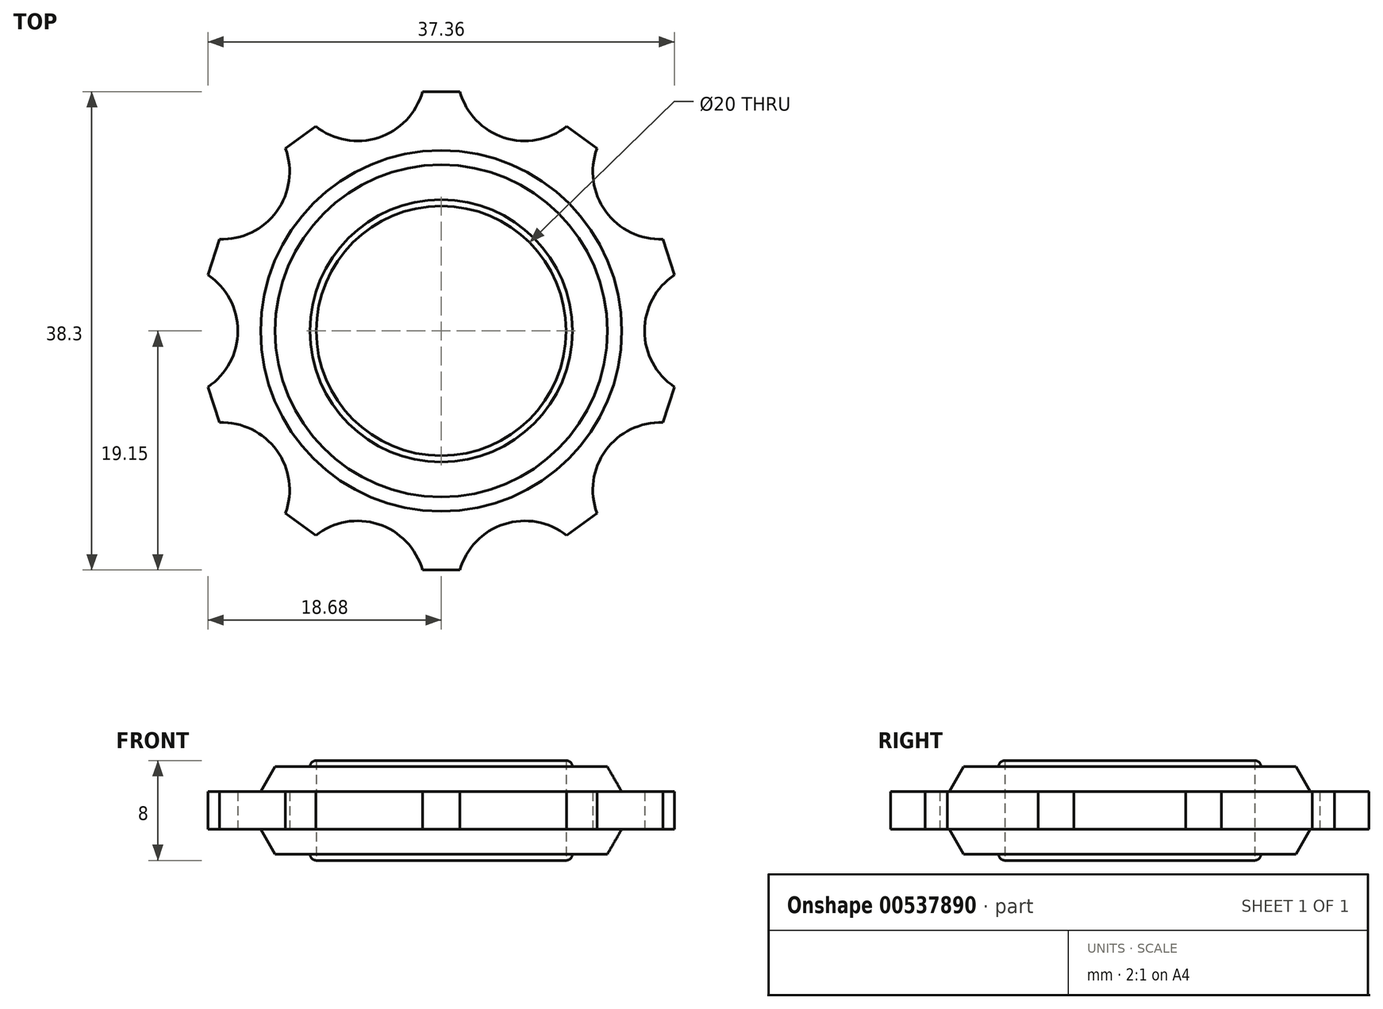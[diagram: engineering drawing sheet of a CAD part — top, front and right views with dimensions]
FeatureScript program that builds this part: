
annotation { "Feature Type Name" : "Feature", "Feature Type Description" : "" }
export const myFeature = defineFeature(function(context is Context, id is Id, definition is map)
    precondition{}
    {
        {
            var Q0;
            Q0=qCreatedBy(makeId("Top.planeOp"),FACE);
            var sketch = newSketch(context, id + "F0", { "sketchPlane" : qUnion([Q0])});
            skCircle(sketch, "E0.cCircle", {"center": v(0, 0) * mm, "radius": 16.27 * mm, "construction": true});
            skLineSegment(sketch, "E0.0", {"start": v(16.27, 5.29) * mm, "end": v(16.27, -5.29) * mm, "construction": true});
            skLineSegment(sketch, "E0.1", {"start": v(16.27, -5.29) * mm, "end": v(10.06, -13.84) * mm, "construction": true});
            skLineSegment(sketch, "E0.2", {"start": v(10.06, -13.84) * mm, "end": v(0, -17.11) * mm, "construction": true});
            skLineSegment(sketch, "E0.3", {"start": v(0, -17.11) * mm, "end": v(-10.06, -13.84) * mm, "construction": true});
            skLineSegment(sketch, "E0.4", {"start": v(-10.06, -13.84) * mm, "end": v(-16.27, -5.29) * mm, "construction": true});
            skLineSegment(sketch, "E0.5", {"start": v(-16.27, -5.29) * mm, "end": v(-16.27, 5.29) * mm, "construction": true});
            skLineSegment(sketch, "E0.6", {"start": v(-16.28, 5.29) * mm, "end": v(-10.06, 13.84) * mm, "construction": true});
            skLineSegment(sketch, "E0.7", {"start": v(-10.06, 13.84) * mm, "end": v(0, 17.11) * mm, "construction": true});
            skLineSegment(sketch, "E0.8", {"start": v(0, 17.11) * mm, "end": v(10.06, 13.84) * mm, "construction": true});
            skLineSegment(sketch, "E0.9", {"start": v(10.06, 13.84) * mm, "end": v(16.27, 5.29) * mm, "construction": true});
            skPoint(sketch, "E0.0.midPoint", {"position": v(16.27, 0) * mm});
            skCircle(sketch, "E1", {"center": v(0, 0) * mm, "radius": 19.15 * mm, "construction": true});
            skLineSegment(sketch, "E2", {"start": v(0, 0) * mm, "end": v(-16.27, -5.29) * mm, "construction": true});
            skLineSegment(sketch, "E3", {"start": v(-16.27, -5.29) * mm, "end": v(-18.21, -5.92) * mm, "construction": true});
            skLineSegment(sketch, "E4", {"start": v(0, 0) * mm, "end": v(-10.06, -13.84) * mm, "construction": true});
            skLineSegment(sketch, "E5", {"start": v(-10.06, -13.84) * mm, "end": v(-11.26, -15.5) * mm, "construction": true});
            skLineSegment(sketch, "E6", {"start": v(0, 0) * mm, "end": v(0, -17.11) * mm, "construction": true});
            skLineSegment(sketch, "E7", {"start": v(0, -17.11) * mm, "end": v(0, -19.15) * mm, "construction": true});
            skLineSegment(sketch, "E8", {"start": v(0, 0) * mm, "end": v(10.06, -13.84) * mm, "construction": true});
            skLineSegment(sketch, "E9", {"start": v(10.06, -13.84) * mm, "end": v(11.26, -15.5) * mm, "construction": true});
            skLineSegment(sketch, "E10", {"start": v(0, 0) * mm, "end": v(16.27, -5.29) * mm, "construction": true});
            skLineSegment(sketch, "E11", {"start": v(16.27, -5.29) * mm, "end": v(18.21, -5.92) * mm, "construction": true});
            skLineSegment(sketch, "E12", {"start": v(0, 0) * mm, "end": v(16.27, 5.29) * mm, "construction": true});
            skLineSegment(sketch, "E13", {"start": v(16.27, 5.29) * mm, "end": v(18.21, 5.92) * mm, "construction": true});
            skLineSegment(sketch, "E14", {"start": v(0, 0) * mm, "end": v(10.06, 13.84) * mm, "construction": true});
            skLineSegment(sketch, "E15", {"start": v(10.06, 13.84) * mm, "end": v(11.26, 15.5) * mm, "construction": true});
            skLineSegment(sketch, "E16", {"start": v(0, 0) * mm, "end": v(0, 17.11) * mm, "construction": true});
            skLineSegment(sketch, "E17", {"start": v(0, 17.11) * mm, "end": v(0, 19.15) * mm, "construction": true});
            skLineSegment(sketch, "E18", {"start": v(0, 0) * mm, "end": v(-10.06, 13.84) * mm, "construction": true});
            skLineSegment(sketch, "E19", {"start": v(-10.06, 13.84) * mm, "end": v(-11.26, 15.5) * mm, "construction": true});
            skLineSegment(sketch, "E20", {"start": v(0, 0) * mm, "end": v(-16.27, 5.29) * mm, "construction": true});
            skLineSegment(sketch, "E21", {"start": v(-16.28, 5.29) * mm, "end": v(-18.21, 5.92) * mm, "construction": true});
            skPoint(sketch, "E22.0.midPoint", {"position": v(0, 19.15) * mm});
            skLineSegment(sketch, "E23", {"start": v(-18.21, 5.92) * mm, "end": v(-18.68, 4.5) * mm});
            skLineSegment(sketch, "E24", {"start": v(-18.21, 5.92) * mm, "end": v(-17.75, 7.34) * mm});
            skLineSegment(sketch, "E25.0", {"start": v(16.27, 0) * mm, "end": v(13.17, -9.57) * mm, "construction": true});
            skLineSegment(sketch, "E25.1", {"start": v(13.17, -9.57) * mm, "end": v(5.03, -15.48) * mm, "construction": true});
            skLineSegment(sketch, "E25.2", {"start": v(5.03, -15.48) * mm, "end": v(-5.03, -15.48) * mm, "construction": true});
            skLineSegment(sketch, "E25.3", {"start": v(-5.03, -15.48) * mm, "end": v(-13.17, -9.57) * mm, "construction": true});
            skLineSegment(sketch, "E25.4", {"start": v(-13.17, -9.57) * mm, "end": v(-16.27, 0) * mm, "construction": true});
            skLineSegment(sketch, "E25.5", {"start": v(-16.27, 0) * mm, "end": v(-13.17, 9.57) * mm, "construction": true});
            skLineSegment(sketch, "E25.6", {"start": v(-13.17, 9.57) * mm, "end": v(-5.03, 15.48) * mm, "construction": true});
            skLineSegment(sketch, "E25.7", {"start": v(-5.03, 15.48) * mm, "end": v(5.03, 15.48) * mm, "construction": true});
            skLineSegment(sketch, "E25.8", {"start": v(5.03, 15.48) * mm, "end": v(13.17, 9.57) * mm, "construction": true});
            skLineSegment(sketch, "E25.9", {"start": v(13.17, 9.57) * mm, "end": v(16.27, 0) * mm, "construction": true});
            skLineSegment(sketch, "E26", {"start": v(-11.26, 15.5) * mm, "end": v(-12.47, 14.61) * mm});
            skArc(sketch, "E27", {"start": v(-17.75, 7.34) * mm, "mid": v(-13.17, 9.57) * mm, "end": v(-12.47, 14.61) * mm});
            skLineSegment(sketch, "E28", {"start": v(-11.26, 15.5) * mm, "end": v(-10.04, 16.37) * mm});
            skLineSegment(sketch, "E29", {"start": v(0, 19.15) * mm, "end": v(-1.5, 19.15) * mm});
            skLineSegment(sketch, "E30", {"start": v(0, 19.15) * mm, "end": v(1.5, 19.15) * mm});
            skLineSegment(sketch, "E31", {"start": v(11.26, 15.5) * mm, "end": v(10.04, 16.37) * mm});
            skLineSegment(sketch, "E32", {"start": v(11.26, 15.5) * mm, "end": v(12.47, 14.61) * mm});
            skLineSegment(sketch, "E33", {"start": v(18.21, 5.92) * mm, "end": v(17.75, 7.34) * mm});
            skLineSegment(sketch, "E34", {"start": v(18.21, 5.92) * mm, "end": v(18.68, 4.5) * mm});
            skLineSegment(sketch, "E35", {"start": v(18.21, -5.92) * mm, "end": v(18.68, -4.5) * mm});
            skLineSegment(sketch, "E36", {"start": v(18.21, -5.92) * mm, "end": v(17.75, -7.34) * mm});
            skLineSegment(sketch, "E37", {"start": v(11.26, -15.5) * mm, "end": v(12.47, -14.61) * mm});
            skLineSegment(sketch, "E38", {"start": v(11.26, -15.5) * mm, "end": v(10.04, -16.37) * mm});
            skLineSegment(sketch, "E39", {"start": v(0, -19.15) * mm, "end": v(1.5, -19.15) * mm});
            skLineSegment(sketch, "E40", {"start": v(0, -19.15) * mm, "end": v(-1.5, -19.15) * mm});
            skLineSegment(sketch, "E41", {"start": v(-11.26, -15.5) * mm, "end": v(-10.04, -16.37) * mm});
            skLineSegment(sketch, "E42", {"start": v(-11.26, -15.5) * mm, "end": v(-12.47, -14.61) * mm});
            skLineSegment(sketch, "E43", {"start": v(-18.21, -5.92) * mm, "end": v(-17.75, -7.34) * mm});
            skLineSegment(sketch, "E44", {"start": v(-18.21, -5.92) * mm, "end": v(-18.68, -4.5) * mm});
            skArc(sketch, "E45", {"start": v(-10.04, 16.37) * mm, "mid": v(-5.03, 15.48) * mm, "end": v(-1.5, 19.15) * mm});
            skArc(sketch, "E46", {"start": v(1.5, 19.15) * mm, "mid": v(5.03, 15.48) * mm, "end": v(10.04, 16.37) * mm});
            skArc(sketch, "E47", {"start": v(12.47, 14.61) * mm, "mid": v(13.17, 9.57) * mm, "end": v(17.75, 7.34) * mm});
            skArc(sketch, "E48", {"start": v(18.68, 4.5) * mm, "mid": v(16.27, 0) * mm, "end": v(18.68, -4.5) * mm});
            skArc(sketch, "E49", {"start": v(17.75, -7.34) * mm, "mid": v(13.17, -9.57) * mm, "end": v(12.47, -14.61) * mm});
            skArc(sketch, "E50", {"start": v(10.04, -16.37) * mm, "mid": v(5.03, -15.48) * mm, "end": v(1.5, -19.15) * mm});
            skArc(sketch, "E51", {"start": v(-1.5, -19.15) * mm, "mid": v(-5.03, -15.48) * mm, "end": v(-10.04, -16.37) * mm});
            skArc(sketch, "E52", {"start": v(-12.47, -14.61) * mm, "mid": v(-13.17, -9.57) * mm, "end": v(-17.75, -7.34) * mm});
            skArc(sketch, "E53", {"start": v(-18.68, -4.5) * mm, "mid": v(-16.27, 0) * mm, "end": v(-18.68, 4.5) * mm});
            skCircle(sketch, "E54", {"center": v(0, 0) * mm, "radius": 14.5 * mm});
            skCircle(sketch, "E55", {"center": v(0, 0) * mm, "radius": 10.5 * mm});
            skCircle(sketch, "E56", {"center": v(0, 0) * mm, "radius": 10 * mm});
            skCircle(sketch, "E57", {"center": v(0, 0) * mm, "radius": 2.5 * mm});
            skSolve(sketch);
        }
        {
            var Q0;
            Q0=makeQuery(id+"F0.imprint","IMPRINT",FACE,{"disambiguationData":[TD([[makeQuery(id+"F0.imprint","IMPRINT",EDGE,{"derivedFrom":sQuery(id+"F0.wireOp",EDGE,"E23")}),1.0]])]});
            extrude(context, id + "F1", {"entities" : qUnion([Q0]), "depth" : 1.5 * mm, "offsetDistance" : 25 * mm});
        }
        {
            var Q0;
            Q0=makeQuery(id+"F0.imprint","IMPRINT",FACE,{"disambiguationData":[TD([[makeQuery(id+"F0.imprint","IMPRINT",EDGE,{"derivedFrom":sQuery(id+"F0.wireOp",EDGE,"E54")}),1.0]])]});
            extrude(context, id + "F2", {"entities" : qUnion([Q0]), "operationType" : NewBodyOperationType.ADD, "depth" : 3.5 * mm, "offsetDistance" : 25 * mm});
        }
        {
            var Q0;
            Q0=makeQuery(id+"F0.imprint","IMPRINT",FACE,{"disambiguationData":[TD([[makeQuery(id+"F0.imprint","IMPRINT",EDGE,{"derivedFrom":sQuery(id+"F0.wireOp",EDGE,"E55")}),1.0]])]});
            extrude(context, id + "F3", {"entities" : qUnion([Q0]), "operationType" : NewBodyOperationType.ADD, "depth" : 4 * mm, "offsetDistance" : 25 * mm});
        }
        {
            var Q0;
            Q0=makeQuery(id+"F2.opExtrude","CAP_EDGE",EDGE,{"disambiguationData":[OSD([sQuery(id+"F0.wireOp",EDGE,"E54")])],"isStart":false});
            chamfer(context, id + "F4", {"entities" : qUnion([Q0]), "chamferType" : ChamferType.OFFSET_ANGLE, "width" : 1.2 * mm, "oppositeDirection" : false, "angle" : 60 * degree, "tangentPropagation" : true});
        }
        {
            var Q0;
            Q0=makeQuery(id+"F3.opExtrude","CAP_EDGE",EDGE,{"disambiguationData":[OSD([sQuery(id+"F0.wireOp",EDGE,"E55")])],"isStart":false});
            fillet(context, id + "F5", {"entities" : qUnion([Q0]), "radius" : 0.5 * mm, "tangentPropagation" : true, "allowEdgeOverflow" : false});
        }
        {
            var Q0;
            Q0=makeQuery(id+"F1.opExtrude","SWEPT_BODY",BODY,{"disambiguationData":[OSD([sQuery(id+"F0.wireOp",EDGE,"E23"),sQuery(id+"F0.wireOp",EDGE,"E24"),sQuery(id+"F0.wireOp",EDGE,"E26"),sQuery(id+"F0.wireOp",EDGE,"E27"),sQuery(id+"F0.wireOp",EDGE,"E28"),sQuery(id+"F0.wireOp",EDGE,"E29"),sQuery(id+"F0.wireOp",EDGE,"E30"),sQuery(id+"F0.wireOp",EDGE,"E31"),sQuery(id+"F0.wireOp",EDGE,"E32"),sQuery(id+"F0.wireOp",EDGE,"E33"),sQuery(id+"F0.wireOp",EDGE,"E34"),sQuery(id+"F0.wireOp",EDGE,"E35"),sQuery(id+"F0.wireOp",EDGE,"E36"),sQuery(id+"F0.wireOp",EDGE,"E37"),sQuery(id+"F0.wireOp",EDGE,"E38"),sQuery(id+"F0.wireOp",EDGE,"E39"),sQuery(id+"F0.wireOp",EDGE,"E40"),sQuery(id+"F0.wireOp",EDGE,"E41"),sQuery(id+"F0.wireOp",EDGE,"E42"),sQuery(id+"F0.wireOp",EDGE,"E43"),sQuery(id+"F0.wireOp",EDGE,"E44"),sQuery(id+"F0.wireOp",EDGE,"E45"),sQuery(id+"F0.wireOp",EDGE,"E46"),sQuery(id+"F0.wireOp",EDGE,"E47"),sQuery(id+"F0.wireOp",EDGE,"E48"),sQuery(id+"F0.wireOp",EDGE,"E49"),sQuery(id+"F0.wireOp",EDGE,"E50"),sQuery(id+"F0.wireOp",EDGE,"E51"),sQuery(id+"F0.wireOp",EDGE,"E52"),sQuery(id+"F0.wireOp",EDGE,"E53"),sQuery(id+"F0.wireOp",EDGE,"E54")])]});
            var Q1;
            {var subQ0=sQuery(id+"F0.wireOp",EDGE,"E55");var subQ1=sQuery(id+"F0.wireOp",EDGE,"E54");Q1=makeQuery(id+"F3.boolean.opBoolean","MERGE",FACE,{"derivedFrom":[makeQuery(id+"F2.boolean.opBoolean","MERGE",FACE,{"derivedFrom":[makeQuery(id+"F1.opExtrude","CAP_FACE",FACE,{"disambiguationData":[OSD([sQuery(id+"F0.wireOp",EDGE,"E23"),sQuery(id+"F0.wireOp",EDGE,"E24"),sQuery(id+"F0.wireOp",EDGE,"E26"),sQuery(id+"F0.wireOp",EDGE,"E27"),sQuery(id+"F0.wireOp",EDGE,"E28"),sQuery(id+"F0.wireOp",EDGE,"E29"),sQuery(id+"F0.wireOp",EDGE,"E30"),sQuery(id+"F0.wireOp",EDGE,"E31"),sQuery(id+"F0.wireOp",EDGE,"E32"),sQuery(id+"F0.wireOp",EDGE,"E33"),sQuery(id+"F0.wireOp",EDGE,"E34"),sQuery(id+"F0.wireOp",EDGE,"E35"),sQuery(id+"F0.wireOp",EDGE,"E36"),sQuery(id+"F0.wireOp",EDGE,"E37"),sQuery(id+"F0.wireOp",EDGE,"E38"),sQuery(id+"F0.wireOp",EDGE,"E39"),sQuery(id+"F0.wireOp",EDGE,"E40"),sQuery(id+"F0.wireOp",EDGE,"E41"),sQuery(id+"F0.wireOp",EDGE,"E42"),sQuery(id+"F0.wireOp",EDGE,"E43"),sQuery(id+"F0.wireOp",EDGE,"E44"),sQuery(id+"F0.wireOp",EDGE,"E45"),sQuery(id+"F0.wireOp",EDGE,"E46"),sQuery(id+"F0.wireOp",EDGE,"E47"),sQuery(id+"F0.wireOp",EDGE,"E48"),sQuery(id+"F0.wireOp",EDGE,"E49"),sQuery(id+"F0.wireOp",EDGE,"E50"),sQuery(id+"F0.wireOp",EDGE,"E51"),sQuery(id+"F0.wireOp",EDGE,"E52"),sQuery(id+"F0.wireOp",EDGE,"E53"),subQ1])],"isStart":true}),makeQuery(id+"F2.opExtrude","CAP_FACE",FACE,{"disambiguationData":[OSD([subQ1,subQ0])],"isStart":true})]}),makeQuery(id+"F3.opExtrude","CAP_FACE",FACE,{"disambiguationData":[OSD([subQ0,sQuery(id+"F0.wireOp",EDGE,"E56")])],"isStart":true})]});}
            mirror(context, id + "F6", {"operationType" : NewBodyOperationType.ADD, "entities" : qUnion([Q0]), "mirrorPlane" : qUnion([Q1])});
        }
    });
